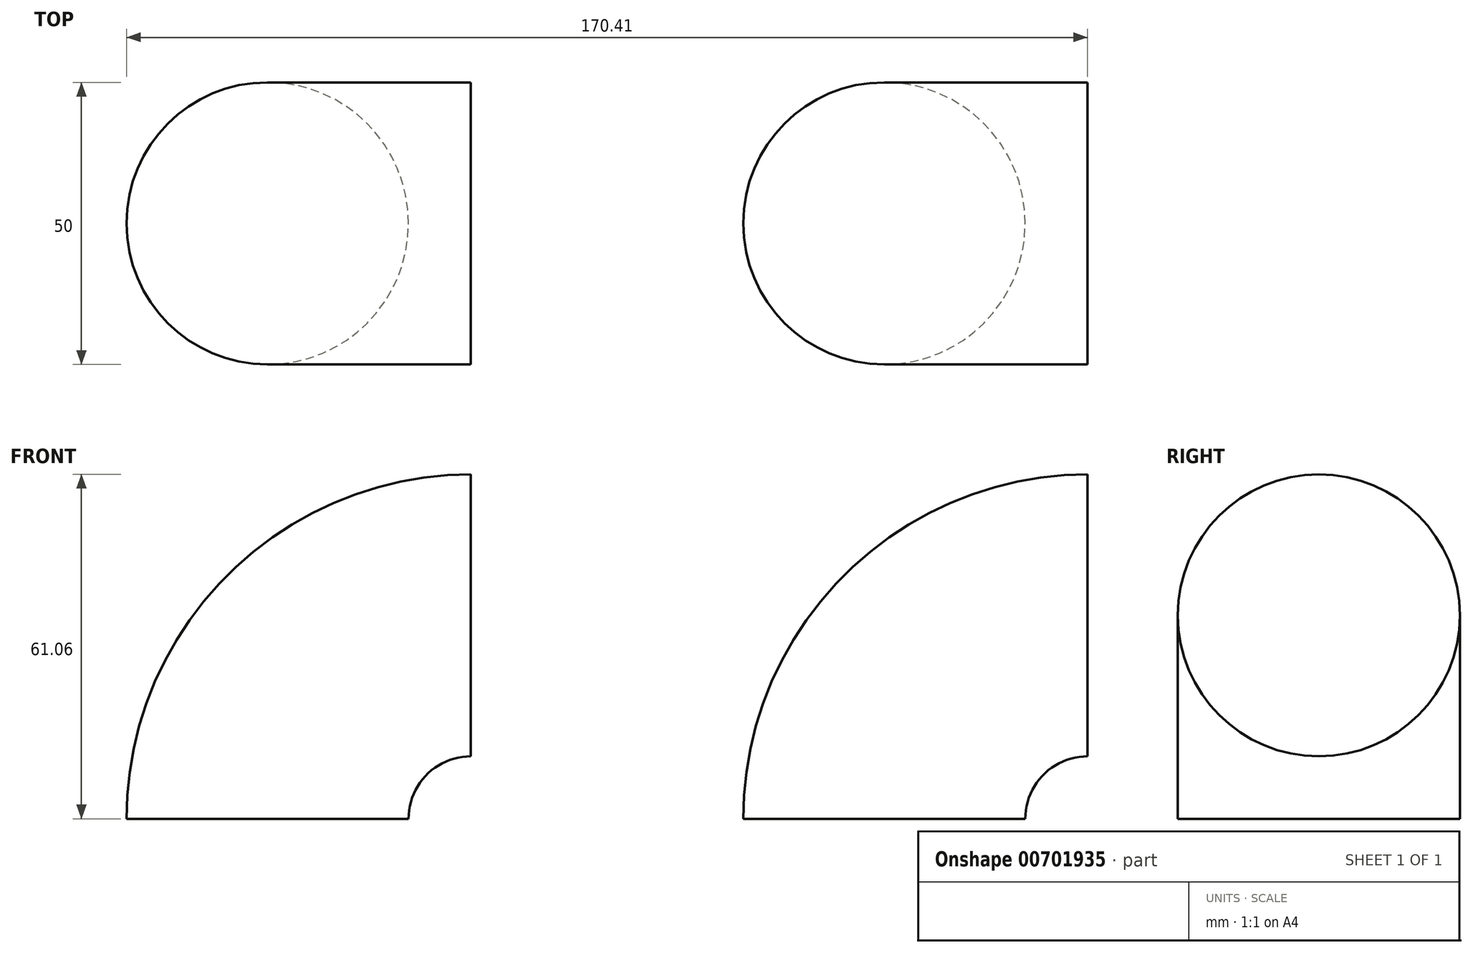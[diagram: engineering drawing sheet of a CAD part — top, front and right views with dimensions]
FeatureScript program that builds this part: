
annotation { "Feature Type Name" : "Feature", "Feature Type Description" : "" }
export const myFeature = defineFeature(function(context is Context, id is Id, definition is map)
    precondition{}
    {
        {
            var Q0;
            Q0=qCreatedBy(makeId("Top.planeOp"),FACE);
            var sketch = newSketch(context, id + "F0", { "sketchPlane" : qUnion([Q0])});
            skCircle(sketch, "E0", {"center": v(0, 0) * mm, "radius": 25 * mm});
            skSolve(sketch);
        }
        {
            var Q0;
            Q0=qCreatedBy(makeId("Front.planeOp"),FACE);
            var sketch = newSketch(context, id + "F1", { "sketchPlane" : qUnion([Q0])});
            skArc(sketch, "E1", {"start": v(0, 0) * mm, "mid": v(10.56, 25.5) * mm, "end": v(36.06, 36.06) * mm});
            skSolve(sketch);
        }
        {
            var Q0;
            Q0=makeQuery(id+"F0.imprint","IMPRINT",FACE,{"disambiguationData":[TD([[makeQuery(id+"F0.imprint","IMPRINT",EDGE,{"derivedFrom":sQuery(id+"F0.wireOp",EDGE,"E0")}),1.0]])]});
            var Q1;
            Q1=sQuery(id+"F1.wireOp",EDGE,"E1");
            sweep(context, id + "F2", {"profiles" : qUnion([Q0]), "path" : qUnion([Q1])});
        }
        {
            var Q0;
            Q0=qCreatedBy(makeId("Top.planeOp"),FACE);
            var sketch = newSketch(context, id + "F3", { "sketchPlane" : qUnion([Q0])});
            skCircle(sketch, "E2", {"center": v(109.35, 0) * mm, "radius": 25 * mm});
            skSolve(sketch);
        }
        {
            var Q0;
            Q0=qCreatedBy(makeId("Front.planeOp"),FACE);
            var sketch = newSketch(context, id + "F4", { "sketchPlane" : qUnion([Q0])});
            skArc(sketch, "E3", {"start": v(109.35, 0) * mm, "mid": v(119.91, 25.5) * mm, "end": v(145.41, 36.06) * mm});
            skSolve(sketch);
        }
        {
            var Q0;
            Q0=makeQuery(id+"F3.imprint","IMPRINT",FACE,{"disambiguationData":[TD([[makeQuery(id+"F3.imprint","IMPRINT",EDGE,{"derivedFrom":sQuery(id+"F3.wireOp",EDGE,"E2")}),1.0]])]});
            var Q1;
            Q1=sQuery(id+"F4.wireOp",EDGE,"E3");
            sweep(context, id + "F5", {"profiles" : qUnion([Q0]), "path" : qUnion([Q1])});
        }
    });
